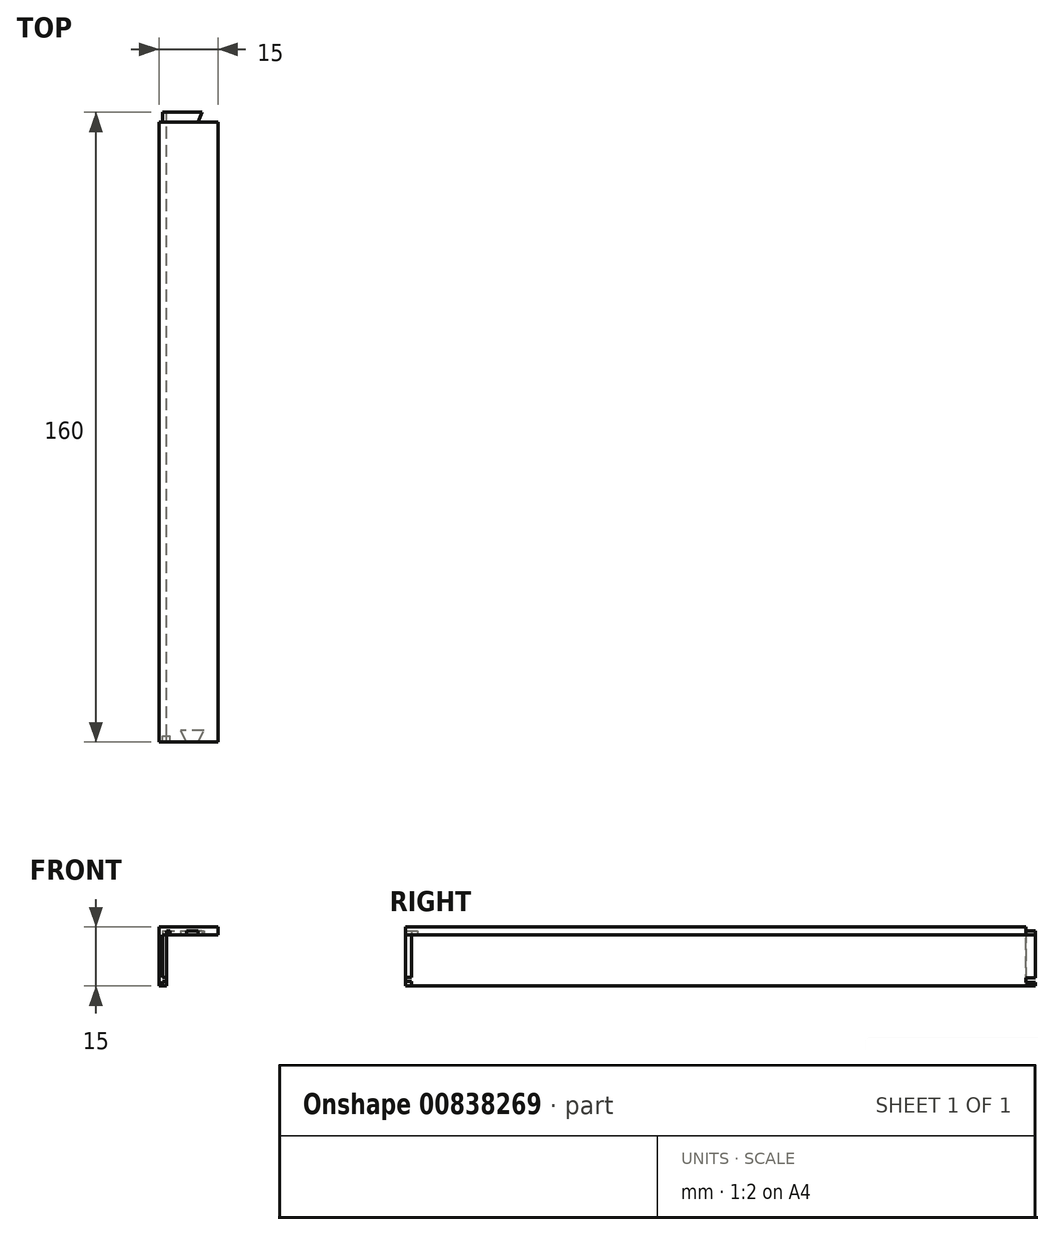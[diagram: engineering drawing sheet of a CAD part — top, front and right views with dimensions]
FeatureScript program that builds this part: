
annotation { "Feature Type Name" : "Feature", "Feature Type Description" : "" }
export const myFeature = defineFeature(function(context is Context, id is Id, definition is map)
    precondition{}
    {
        {
            var Q0;
            Q0=qCreatedBy(makeId("Front.planeOp"),FACE);
            var sketch = newSketch(context, id + "F0", { "sketchPlane" : qUnion([Q0])});
            skLineSegment(sketch, "E0.bottom", {"start": v(0, 0) * mm, "end": v(15, 0) * mm});
            skLineSegment(sketch, "E0.top", {"start": v(0, -2) * mm, "end": v(15, -2) * mm});
            skLineSegment(sketch, "E0.left", {"start": v(0, 0) * mm, "end": v(0, -2) * mm});
            skLineSegment(sketch, "E0.right", {"start": v(15, 0) * mm, "end": v(15, -2) * mm});
            skLineSegment(sketch, "E1.bottom", {"start": v(0, -2) * mm, "end": v(2, -2) * mm});
            skLineSegment(sketch, "E1.top", {"start": v(0, -15) * mm, "end": v(2, -15) * mm});
            skLineSegment(sketch, "E1.left", {"start": v(0, -2) * mm, "end": v(0, -15) * mm});
            skLineSegment(sketch, "E1.right", {"start": v(2, -2) * mm, "end": v(2, -15) * mm});
            skSolve(sketch);
        }
        {
            var Q0;
            Q0 = qSketchRegion(id + "F0", true);
            extrude(context, id + "F1", {"entities" : qUnion([Q0]), "depth" : 160 * mm, "offsetDistance" : 25 * mm});
        }
        {
            var Q0;
            Q0=makeQuery(id+"F1.opExtrude","SWEPT_FACE",FACE,{"disambiguationData":[OSD([sQuery(id+"F0.wireOp",EDGE,"E1.right")])]});
            var sketch = newSketch(context, id + "F2", { "sketchPlane" : qUnion([Q0])});
            skLineSegment(sketch, "E2.bottom", {"start": v(-160, -15) * mm, "end": v(-158.5, -15) * mm});
            skLineSegment(sketch, "E2.top", {"start": v(-160, -13.8) * mm, "end": v(-158.5, -13.8) * mm});
            skLineSegment(sketch, "E2.left", {"start": v(-160, -15) * mm, "end": v(-160, -13.8) * mm});
            skLineSegment(sketch, "E2.right", {"start": v(-158.5, -15) * mm, "end": v(-158.5, -13.8) * mm});
            skLineSegment(sketch, "E3.bottom", {"start": v(-160, -12.8) * mm, "end": v(-158.5, -12.8) * mm});
            skLineSegment(sketch, "E3.top", {"start": v(-160, -2) * mm, "end": v(-158.5, -2) * mm});
            skLineSegment(sketch, "E3.left", {"start": v(-160, -12.8) * mm, "end": v(-160, -2) * mm});
            skLineSegment(sketch, "E3.right", {"start": v(-158.5, -12.8) * mm, "end": v(-158.5, -2) * mm});
            skSolve(sketch);
        }
        {
            var Q0;
            Q0 = qSketchRegion(id + "F2", true);
            extrude(context, id + "F3", {"entities" : qUnion([Q0]), "operationType" : NewBodyOperationType.REMOVE, "oppositeDirection" : true, "depth" : 1 * mm, "offsetDistance" : 25 * mm});
        }
        {
            var Q0;
            Q0=makeQuery(id+"F1.opExtrude","SWEPT_FACE",FACE,{"disambiguationData":[OSD([sQuery(id+"F0.wireOp",EDGE,"E0.top")])]});
            var sketch = newSketch(context, id + "F4", { "sketchPlane" : qUnion([Q0])});
            skLineSegment(sketch, "E4.MirrorCS", {"start": v(10, 160) * mm, "end": v(11.5, 157) * mm});
            skLineSegment(sketch, "E5.MirrorCS", {"start": v(11.5, 157) * mm, "end": v(5.5, 157) * mm});
            skLineSegment(sketch, "E6.MirrorCS", {"start": v(5.5, 157) * mm, "end": v(7, 160) * mm});
            skLineSegment(sketch, "E7.MirrorCS", {"start": v(7, 160) * mm, "end": v(10, 160) * mm});
            skLineSegment(sketch, "E8.bottom", {"start": v(2, 160) * mm, "end": v(2.8, 160) * mm});
            skLineSegment(sketch, "E8.top", {"start": v(2, 158.5) * mm, "end": v(2.8, 158.5) * mm});
            skLineSegment(sketch, "E8.left", {"start": v(2, 160) * mm, "end": v(2, 158.5) * mm});
            skLineSegment(sketch, "E8.right", {"start": v(2.8, 160) * mm, "end": v(2.8, 158.5) * mm});
            skSolve(sketch);
        }
        {
            var Q0;
            Q0 = qSketchRegion(id + "F4", true);
            extrude(context, id + "F5", {"entities" : qUnion([Q0]), "operationType" : NewBodyOperationType.REMOVE, "oppositeDirection" : true, "depth" : 1 * mm, "offsetDistance" : 25 * mm});
        }
        {
            var Q0;
            Q0=makeQuery(id+"F1.opExtrude","SWEPT_FACE",FACE,{"disambiguationData":[OSD([sQuery(id+"F0.wireOp",EDGE,"E0.top")])]});
            var sketch = newSketch(context, id + "F6", { "sketchPlane" : qUnion([Q0])});
            skLineSegment(sketch, "E9", {"start": v(11, 0) * mm, "end": v(10, 2.5) * mm});
            skLineSegment(sketch, "E10", {"start": v(10, 2.5) * mm, "end": v(7, 2.5) * mm});
            skLineSegment(sketch, "E11", {"start": v(7, 2.5) * mm, "end": v(6, 0) * mm});
            skLineSegment(sketch, "E12", {"start": v(6, 0) * mm, "end": v(11, 0) * mm});
            skLineSegment(sketch, "E13.bottom", {"start": v(7, 2.5) * mm, "end": v(15, 2.5) * mm});
            skLineSegment(sketch, "E13.top", {"start": v(7, 0) * mm, "end": v(15, 0) * mm});
            skLineSegment(sketch, "E13.left", {"start": v(7, 2.5) * mm, "end": v(7, 0) * mm});
            skLineSegment(sketch, "E13.right", {"start": v(15, 2.5) * mm, "end": v(15, 0) * mm});
            skLineSegment(sketch, "E14", {"start": v(7, 2.5) * mm, "end": v(2, 2.5) * mm});
            skLineSegment(sketch, "E15", {"start": v(2, 2.5) * mm, "end": v(2, 0) * mm});
            skSolve(sketch);
        }
        {
            var Q0;
            {var subQ0=sQuery(id+"F6.wireOp",EDGE,"E9");Q0=makeQuery(id+"F6.imprint","IMPRINT",FACE,{"disambiguationData":[TD([[makeQuery(id+"F6.imprint","IMPRINT",EDGE,{"derivedFrom":subQ0}),-1.0]])]});}
            var Q1;
            {var subQ0=sQuery(id+"F6.wireOp",EDGE,"E11");Q1=makeQuery(id+"F6.imprint","IMPRINT",FACE,{"disambiguationData":[TD([[makeQuery(id+"F6.imprint","IMPRINT",EDGE,{"derivedFrom":subQ0}),-1.0]])]});}
            extrude(context, id + "F7", {"entities" : qUnion([Q0, Q1]), "operationType" : NewBodyOperationType.REMOVE, "oppositeDirection" : true, "depth" : 2 * mm, "offsetDistance" : 25 * mm});
        }
        {
            var Q0;
            Q0=makeQuery(id+"F7.boolean.opBoolean","MERGE",FACE,{"derivedFrom":[makeQuery(id+"F1.opExtrude","SWEPT_FACE",FACE,{"disambiguationData":[OSD([sQuery(id+"F0.wireOp",EDGE,"E1.right")])]}),makeQuery(id+"F7.opExtrude","SWEPT_FACE",FACE,{"disambiguationData":[OSD([sQuery(id+"F6.wireOp",EDGE,"E13.left")])]})]});
            var sketch = newSketch(context, id + "F8", { "sketchPlane" : qUnion([Q0])});
            skLineSegment(sketch, "E16.bottom", {"start": v(-2.5, -2) * mm, "end": v(0, -2) * mm});
            skLineSegment(sketch, "E16.top", {"start": v(-2.5, -14.1) * mm, "end": v(0, -14.1) * mm});
            skLineSegment(sketch, "E16.left", {"start": v(-2.5, -2) * mm, "end": v(-2.5, -14.1) * mm});
            skLineSegment(sketch, "E16.right", {"start": v(0, -2) * mm, "end": v(0, -14.1) * mm});
            skLineSegment(sketch, "E17.bottom", {"start": v(0, -12.9) * mm, "end": v(-2.5, -12.9) * mm});
            skLineSegment(sketch, "E17.top", {"start": v(0, -14.1) * mm, "end": v(-2.5, -14.1) * mm});
            skLineSegment(sketch, "E17.left", {"start": v(0, -12.9) * mm, "end": v(0, -14.1) * mm});
            skLineSegment(sketch, "E17.right", {"start": v(-2.5, -12.9) * mm, "end": v(-2.5, -14.1) * mm});
            skSolve(sketch);
        }
        {
            var Q0;
            Q0=makeQuery(id+"F8.imprint","IMPRINT",FACE,{"disambiguationData":[TD([[makeQuery(id+"F8.imprint","IMPRINT",EDGE,{"derivedFrom":sQuery(id+"F8.wireOp",EDGE,"E17.bottom")}),1.0]])]});
            extrude(context, id + "F9", {"entities" : qUnion([Q0]), "operationType" : NewBodyOperationType.REMOVE, "oppositeDirection" : true, "depth" : 1 * mm, "offsetDistance" : 25 * mm});
        }
        {
            var Q0;
            Q0=makeQuery(id+"F1.opExtrude","SWEPT_FACE",FACE,{"disambiguationData":[OSD([sQuery(id+"F0.wireOp",EDGE,"E0.bottom")])]});
            var sketch = newSketch(context, id + "F10", { "sketchPlane" : qUnion([Q0])});
            skLineSegment(sketch, "E18.bottom", {"start": v(0, 0) * mm, "end": v(11, 0) * mm});
            skLineSegment(sketch, "E18.top", {"start": v(0, -2.5) * mm, "end": v(11, -2.5) * mm});
            skLineSegment(sketch, "E18.left", {"start": v(0, 0) * mm, "end": v(0, -2.5) * mm});
            skLineSegment(sketch, "E18.right", {"start": v(11, 0) * mm, "end": v(11, -2.5) * mm});
            skSolve(sketch);
        }
        {
            var Q0;
            Q0 = qSketchRegion(id + "F10", true);
            extrude(context, id + "F11", {"entities" : qUnion([Q0]), "operationType" : NewBodyOperationType.REMOVE, "oppositeDirection" : true, "depth" : 1 * mm, "offsetDistance" : 25 * mm});
        }
        {
            var Q0;
            Q0=makeQuery(id+"F1.opExtrude","SWEPT_FACE",FACE,{"disambiguationData":[OSD([sQuery(id+"F0.wireOp",EDGE,"E0.left"),sQuery(id+"F0.wireOp",EDGE,"E1.left")])]});
            var sketch = newSketch(context, id + "F12", { "sketchPlane" : qUnion([Q0])});
            skLineSegment(sketch, "E19.bottom", {"start": v(0, -1) * mm, "end": v(2.5, -1) * mm});
            skLineSegment(sketch, "E19.top", {"start": v(0, -15) * mm, "end": v(2.5, -15) * mm});
            skLineSegment(sketch, "E19.left", {"start": v(0, -1) * mm, "end": v(0, -15) * mm});
            skLineSegment(sketch, "E19.right", {"start": v(2.5, -1) * mm, "end": v(2.5, -15) * mm});
            skSolve(sketch);
        }
        {
            var Q0;
            Q0 = qSketchRegion(id + "F12", true);
            extrude(context, id + "F13", {"entities" : qUnion([Q0]), "operationType" : NewBodyOperationType.REMOVE, "oppositeDirection" : true, "depth" : 1 * mm, "offsetDistance" : 25 * mm});
        }
    });
